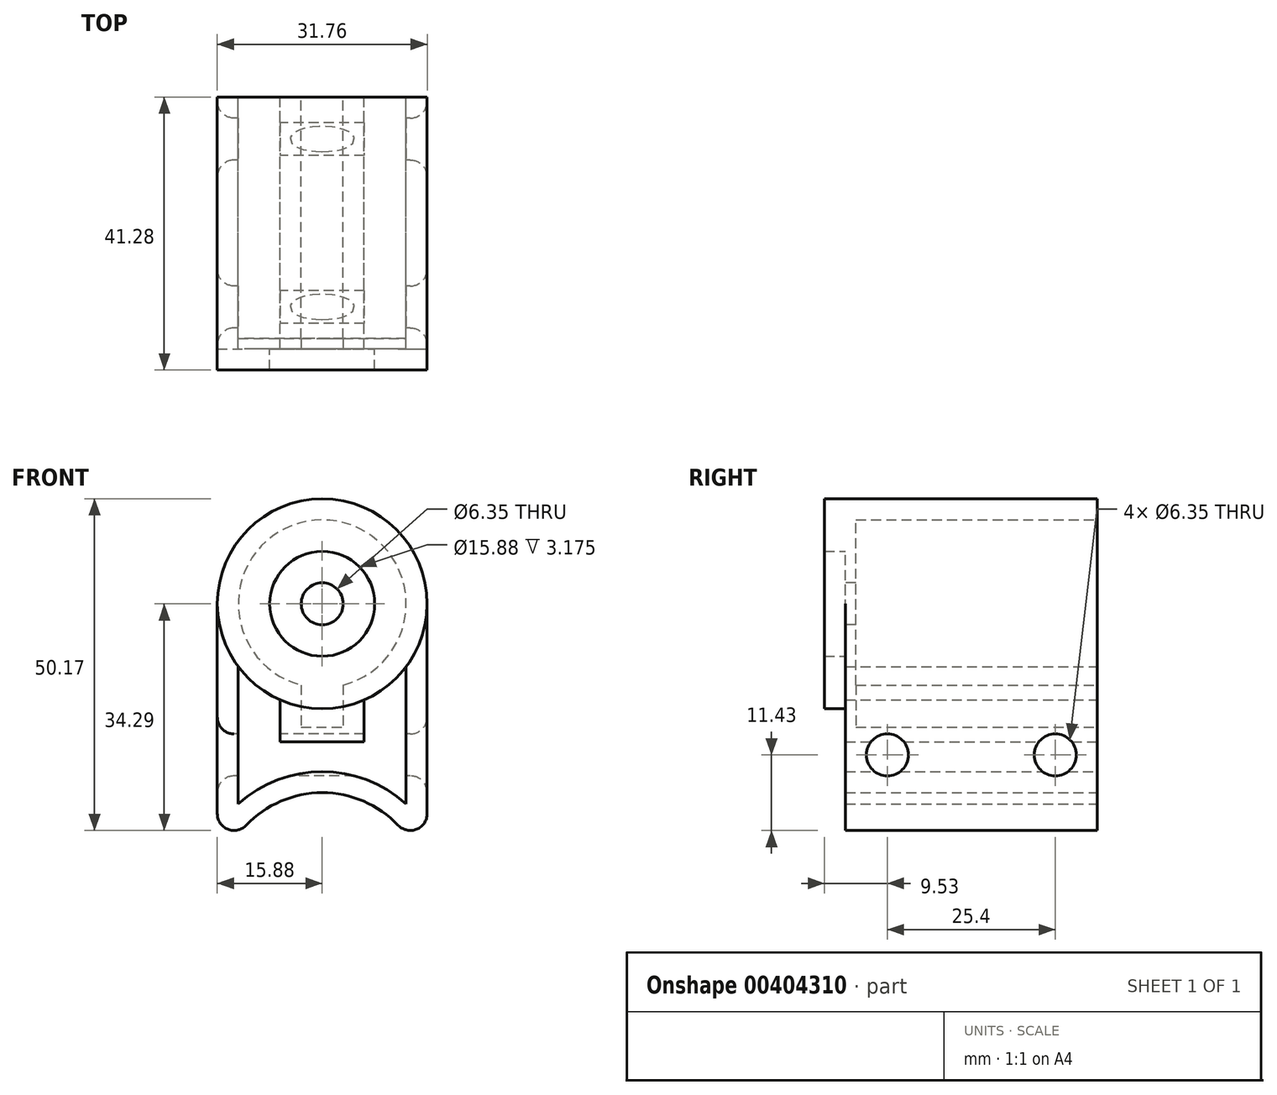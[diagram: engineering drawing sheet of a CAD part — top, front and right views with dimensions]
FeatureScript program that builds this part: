
annotation { "Feature Type Name" : "Feature", "Feature Type Description" : "" }
export const myFeature = defineFeature(function(context is Context, id is Id, definition is map)
    precondition{}
    {
        {
            var Q0;
            Q0=qCreatedBy(makeId("Front.planeOp"),FACE);
            var sketch = newSketch(context, id + "F0", { "sketchPlane" : qUnion([Q0])});
            skCircle(sketch, "E0", {"center": v(0, -44.45) * mm, "radius": 15.88 * mm});
            skLineSegment(sketch, "E1", {"start": v(-15.88, 0) * mm, "end": v(-15.88, -44.45) * mm});
            skLineSegment(sketch, "E2", {"start": v(15.87, 0) * mm, "end": v(15.88, -44.45) * mm});
            skLineSegment(sketch, "E3", {"start": v(-12.7, -9.52) * mm, "end": v(-12.7, -30.25) * mm});
            skLineSegment(sketch, "E4.MirrorCS", {"start": v(12.7, -9.52) * mm, "end": v(12.7, -30.25) * mm});
            skArc(sketch, "E5", {"start": v(12.7, -30.25) * mm, "mid": v(0, -25.4) * mm, "end": v(-12.7, -30.25) * mm});
            skLineSegment(sketch, "E6", {"start": v(0, 0) * mm, "end": v(0, -66.93) * mm, "construction": true});
            skLineSegment(sketch, "E7", {"start": v(-6.35, -14.55) * mm, "end": v(-6.35, -20.9) * mm});
            skLineSegment(sketch, "E8.MirrorCS", {"start": v(6.35, -14.55) * mm, "end": v(6.35, -20.9) * mm});
            skLineSegment(sketch, "E9", {"start": v(-6.35, -20.9) * mm, "end": v(6.35, -20.9) * mm});
            skArc(sketch, "E10", {"start": v(6.35, -14.55) * mm, "mid": v(0, 15.87) * mm, "end": v(-6.35, -14.55) * mm});
            skLineSegment(sketch, "E11", {"start": v(-3.18, -12.3) * mm, "end": v(-3.18, -18.65) * mm});
            skLineSegment(sketch, "E12.MirrorCS", {"start": v(3.18, -12.3) * mm, "end": v(3.18, -12.3) * mm});
            skLineSegment(sketch, "E13", {"start": v(-3.18, -18.65) * mm, "end": v(3.18, -18.65) * mm});
            skLineSegment(sketch, "E14", {"start": v(3.18, -12.3) * mm, "end": v(3.18, -18.65) * mm});
            skArc(sketch, "E15", {"start": v(3.18, -12.3) * mm, "mid": v(0, 12.7) * mm, "end": v(-3.18, -12.3) * mm});
            skSolve(sketch);
        }
        {
            var Q0;
            Q0=makeQuery(id+"F0.imprint","IMPRINT",FACE,{"disambiguationData":[TD([[makeQuery(id+"F0.imprint","IMPRINT",EDGE,{"derivedFrom":sQuery(id+"F0.wireOp",EDGE,"k3dLSpok-UVCr-wi4I-vXE7-o1PV2ETb6fC6")}),-1.0]])]});
            var Q1;
            {var subQ0=sQuery(id+"F0.wireOp",EDGE,"E1");Q1=makeQuery(id+"F0.imprint","IMPRINT",FACE,{"disambiguationData":[TD([[makeQuery(id+"F0.imprint","IMPRINT",EDGE,{"derivedFrom":subQ0}),1.0]])]});}
            var Q2;
            {var subQ2=sQuery(id+"F0.wireOp",EDGE,"E7");Q2=makeQuery(id+"F0.imprint","IMPRINT",FACE,{"disambiguationData":[TD([[makeQuery(id+"F0.imprint","IMPRINT",EDGE,{"derivedFrom":subQ2}),1.0]])]});}
            extrude(context, id + "F1", {"entities" : qUnion([Q0, Q1, Q2]), "depth" : 38.1 * mm});
        }
        {
            var Q0;
            Q0=qCreatedBy(makeId("Right.planeOp"),FACE);
            var sketch = newSketch(context, id + "F2", { "sketchPlane" : qUnion([Q0])});
            skCircle(sketch, "E16", {"center": v(-31.75, -22.86) * mm, "radius": 3.18 * mm});
            skCircle(sketch, "E17", {"center": v(-6.35, -22.86) * mm, "radius": 3.18 * mm});
            skLineSegment(sketch, "E18", {"start": v(0, 0) * mm, "end": v(-100.68, 0) * mm, "construction": true});
            skSolve(sketch);
        }
        {
            var Q0;
            Q0 = qSketchRegion(id + "F2", true);
            extrude(context, id + "F3", {"entities" : qUnion([Q0]), "operationType" : NewBodyOperationType.REMOVE, "endBound" : BoundingType.SYMMETRIC, "depth" : 50.8 * mm});
        }
        {
            var Q0;
            Q0=makeQuery(id+"F1.opExtrude","SWEPT_EDGE",EDGE,{"disambiguationData":[OSD([sQuery(id+"F0.wireOp",EDGE,"E0"),sQuery(id+"F0.wireOp",EDGE,"E2")])]});
            var Q1;
            Q1=makeQuery(id+"F1.opExtrude","SWEPT_EDGE",EDGE,{"disambiguationData":[OSD([sQuery(id+"F0.wireOp",EDGE,"E0"),sQuery(id+"F0.wireOp",EDGE,"E1")])]});
            fillet(context, id + "F4", {"entities" : qUnion([Q0, Q1]), "radius" : 2.54 * mm, "tangentPropagation" : true, "allowEdgeOverflow" : false});
        }
        {
            var Q0;
            Q0=makeQuery(id+"F3.boolean.opBoolean","INTERSECT",EDGE,{"derivedFrom":[makeQuery(id+"F1.opExtrude","SWEPT_FACE",FACE,{"disambiguationData":[OSD([sQuery(id+"F0.wireOp",EDGE,"E1")])]}),makeQuery(id+"F3.opExtrude","SWEPT_FACE",FACE,{"disambiguationData":[OSD([sQuery(id+"F2.wireOp",EDGE,"E17")])]})]});
            var Q1;
            Q1=makeQuery(id+"F3.boolean.opBoolean","INTERSECT",EDGE,{"derivedFrom":[makeQuery(id+"F1.opExtrude","SWEPT_FACE",FACE,{"disambiguationData":[OSD([sQuery(id+"F0.wireOp",EDGE,"E1")])]}),makeQuery(id+"F3.opExtrude","SWEPT_FACE",FACE,{"disambiguationData":[OSD([sQuery(id+"F2.wireOp",EDGE,"E16")])]})]});
            var Q2;
            Q2=makeQuery(id+"F3.boolean.opBoolean","INTERSECT",EDGE,{"derivedFrom":[makeQuery(id+"F1.opExtrude","SWEPT_FACE",FACE,{"disambiguationData":[OSD([sQuery(id+"F0.wireOp",EDGE,"E2")])]}),makeQuery(id+"F3.opExtrude","SWEPT_FACE",FACE,{"disambiguationData":[OSD([sQuery(id+"F2.wireOp",EDGE,"E16")])]})]});
            var Q3;
            Q3=makeQuery(id+"F3.boolean.opBoolean","INTERSECT",EDGE,{"derivedFrom":[makeQuery(id+"F1.opExtrude","SWEPT_FACE",FACE,{"disambiguationData":[OSD([sQuery(id+"F0.wireOp",EDGE,"E2")])]}),makeQuery(id+"F3.opExtrude","SWEPT_FACE",FACE,{"disambiguationData":[OSD([sQuery(id+"F2.wireOp",EDGE,"E17")])]})]});
            var Q4;
            {var subQ0=sQuery(id+"F0.wireOp",EDGE,"BopbSLPy-xGV4-c2H3-rYxS-8TJRNXOkyhZj");Q4=makeQuery(id+"F3.boolean.opBoolean","INTERSECT",EDGE,{"disambiguationData":[OD(1.0)],"derivedFrom":[makeQuery(id+"F1.opExtrude","SWEPT_FACE",FACE,{"disambiguationData":[OSD([subQ0]),TDD([makeQuery(id+"F0.imprint","IMPRINT",EDGE,{"disambiguationData":[TD([[makeQuery(id+"F0.imprint","INTERSECT",VERTEX,{"derivedFrom":[subQ0,sQuery(id+"F0.wireOp",EDGE,"E1")]}),1.0]])],"derivedFrom":subQ0})])]}),makeQuery(id+"F3.opExtrude","SWEPT_FACE",FACE,{"disambiguationData":[OSD([sQuery(id+"F2.wireOp",EDGE,"hnllmpSd-9A2M-P7gu-xSds-7rVqE0HCG1G2")])]})]});}
            var Q5;
            {var subQ0=sQuery(id+"F0.wireOp",EDGE,"BopbSLPy-xGV4-c2H3-rYxS-8TJRNXOkyhZj");Q5=makeQuery(id+"F3.boolean.opBoolean","INTERSECT",EDGE,{"disambiguationData":[OD(1.0)],"derivedFrom":[makeQuery(id+"F1.opExtrude","SWEPT_FACE",FACE,{"disambiguationData":[OSD([subQ0]),TDD([makeQuery(id+"F0.imprint","IMPRINT",EDGE,{"disambiguationData":[TD([[makeQuery(id+"F0.imprint","INTERSECT",VERTEX,{"derivedFrom":[subQ0,sQuery(id+"F0.wireOp",EDGE,"E1")]}),1.0]])],"derivedFrom":subQ0})])]}),makeQuery(id+"F3.opExtrude","SWEPT_FACE",FACE,{"disambiguationData":[OSD([sQuery(id+"F2.wireOp",EDGE,"LThNZfQr-GWgv-jDht-xWCW-xUvrxZUgXr7o")])]})]});}
            fillet(context, id + "F5", {"entities" : qUnion([Q0, Q1, Q2, Q3, Q4, Q5]), "radius" : 2.54 * mm, "tangentPropagation" : true, "allowEdgeOverflow" : false});
        }
        {
            var Q0;
            Q0=makeQuery(id+"F1.opExtrude","CAP_FACE",FACE,{"disambiguationData":[OSD([sQuery(id+"F0.wireOp",EDGE,"E0"),sQuery(id+"F0.wireOp",EDGE,"E1"),sQuery(id+"F0.wireOp",EDGE,"E2"),sQuery(id+"F0.wireOp",EDGE,"E3"),sQuery(id+"F0.wireOp",EDGE,"E4.MirrorCS"),sQuery(id+"F0.wireOp",EDGE,"E5"),sQuery(id+"F0.wireOp",EDGE,"E7"),sQuery(id+"F0.wireOp",EDGE,"E8.MirrorCS"),sQuery(id+"F0.wireOp",EDGE,"E9"),sQuery(id+"F0.wireOp",EDGE,"E10"),sQuery(id+"F0.wireOp",EDGE,"E11"),sQuery(id+"F0.wireOp",EDGE,"E13"),sQuery(id+"F0.wireOp",EDGE,"E14"),sQuery(id+"F0.wireOp",EDGE,"E15")])],"isStart":false});
            var sketch = newSketch(context, id + "F6", { "sketchPlane" : qUnion([Q0])});
            skCircle(sketch, "E19", {"center": v(0, 0) * mm, "radius": 3.18 * mm});
            skLineSegment(sketch, "E20", {"start": v(-6.35, -14.55) * mm, "end": v(-6.35, -20.9) * mm});
            skLineSegment(sketch, "E21", {"start": v(-6.35, -20.9) * mm, "end": v(6.35, -20.9) * mm});
            skLineSegment(sketch, "E22", {"start": v(6.35, -20.9) * mm, "end": v(6.35, -14.55) * mm});
            skArc(sketch, "E23", {"start": v(6.35, -14.55) * mm, "mid": v(0, 15.88) * mm, "end": v(-6.35, -14.55) * mm});
            skSolve(sketch);
        }
        {
            var Q0;
            Q0 = qSketchRegion(id + "F6", true);
            extrude(context, id + "F7", {"entities" : qUnion([Q0]), "operationType" : NewBodyOperationType.ADD, "oppositeDirection" : true, "depth" : 1.59 * mm});
        }
        {
            var Q0;
            Q0=makeQuery(id+"F7.boolean.opBoolean","MERGE",FACE,{"derivedFrom":[makeQuery(id+"F1.opExtrude","CAP_FACE",FACE,{"disambiguationData":[OSD([sQuery(id+"F0.wireOp",EDGE,"E0"),sQuery(id+"F0.wireOp",EDGE,"E1"),sQuery(id+"F0.wireOp",EDGE,"E2"),sQuery(id+"F0.wireOp",EDGE,"E3"),sQuery(id+"F0.wireOp",EDGE,"E4.MirrorCS"),sQuery(id+"F0.wireOp",EDGE,"E5"),sQuery(id+"F0.wireOp",EDGE,"E7"),sQuery(id+"F0.wireOp",EDGE,"E8.MirrorCS"),sQuery(id+"F0.wireOp",EDGE,"E9"),sQuery(id+"F0.wireOp",EDGE,"E10"),sQuery(id+"F0.wireOp",EDGE,"E11"),sQuery(id+"F0.wireOp",EDGE,"E13"),sQuery(id+"F0.wireOp",EDGE,"E14"),sQuery(id+"F0.wireOp",EDGE,"E15")])],"isStart":false}),makeQuery(id+"F7.opExtrude","CAP_FACE",FACE,{"disambiguationData":[OSD([sQuery(id+"F6.wireOp",EDGE,"E19"),sQuery(id+"F6.wireOp",EDGE,"E20"),sQuery(id+"F6.wireOp",EDGE,"E21"),sQuery(id+"F6.wireOp",EDGE,"E22"),sQuery(id+"F6.wireOp",EDGE,"E23")])],"isStart":true})]});
            var sketch = newSketch(context, id + "F8", { "sketchPlane" : qUnion([Q0])});
            skCircle(sketch, "E24", {"center": v(0, 0) * mm, "radius": 7.94 * mm});
            skCircle(sketch, "E25", {"center": v(0, 0) * mm, "radius": 15.88 * mm});
            skSolve(sketch);
        }
        {
            var Q0;
            Q0 = qSketchRegion(id + "F8", true);
            extrude(context, id + "F9", {"entities" : qUnion([Q0]), "operationType" : NewBodyOperationType.ADD, "depth" : 3.17 * mm});
        }
    });
